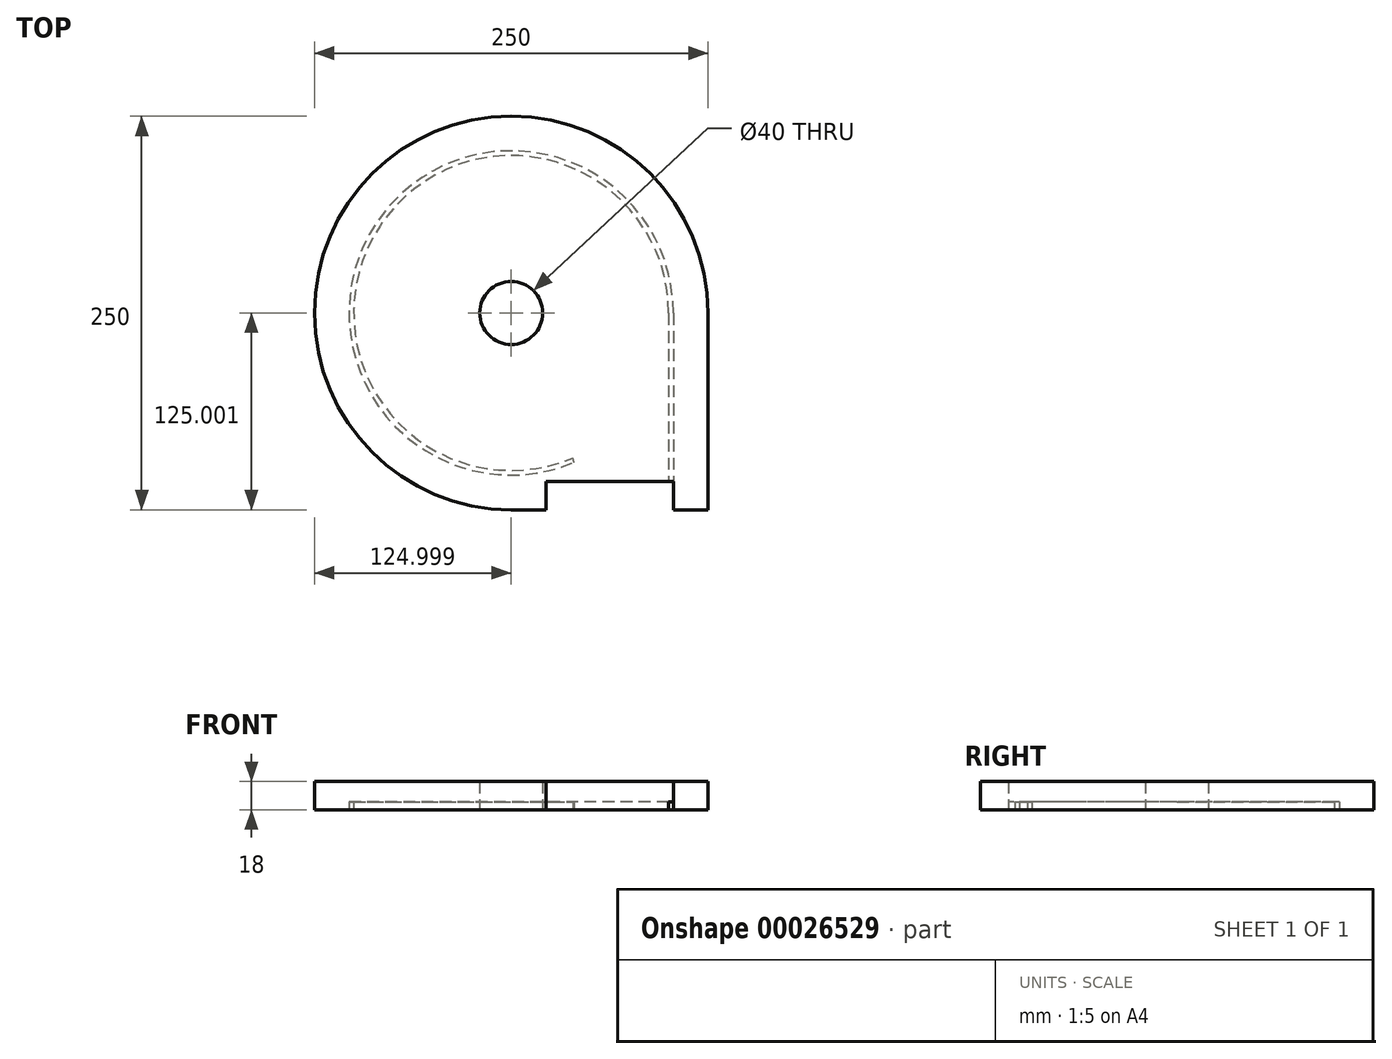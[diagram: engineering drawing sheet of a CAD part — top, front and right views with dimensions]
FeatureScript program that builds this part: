
annotation { "Feature Type Name" : "Feature", "Feature Type Description" : "" }
export const myFeature = defineFeature(function(context is Context, id is Id, definition is map)
    precondition{}
    {
        {
            var Q0;
            Q0=qCreatedBy(makeId("Top.planeOp"),FACE);
            var sketch = newSketch(context, id + "F0", { "sketchPlane" : qUnion([Q0])});
            skArc(sketch, "E0", {"start": v(5.4, 119.39) * mm, "mid": v(-133.76, 46.22) * mm, "end": v(-14.35, -56.06) * mm});
            skArc(sketch, "E1", {"start": v(60.64, 35.6) * mm, "mid": v(-122.78, 90.74) * mm, "end": v(-0.2, -56.42) * mm});
            skLineSegment(sketch, "E2", {"start": v(63.64, 35.6) * mm, "end": v(63.64, -89.4) * mm});
            skLineSegment(sketch, "E3", {"start": v(60.64, 35.6) * mm, "end": v(60.64, -71.4) * mm});
            skLineSegment(sketch, "E4", {"start": v(-17.36, -65.03) * mm, "end": v(-17.36, -89.4) * mm});
            skLineSegment(sketch, "E5", {"start": v(63.64, -71.4) * mm, "end": v(-17.36, -71.4) * mm});
            skLineSegment(sketch, "E6", {"start": v(85.64, 35.6) * mm, "end": v(85.53, -89.4) * mm});
            skLineSegment(sketch, "E7", {"start": v(-6.5, -39.68) * mm, "end": v(-6.91, -38.75) * mm});
            skLineSegment(sketch, "E8", {"start": v(8.8, 100.86) * mm, "end": v(9.4, 101.68) * mm});
            skArc(sketch, "E9", {"start": v(-6.5, 97.4) * mm, "mid": v(-108.92, 43.42) * mm, "end": v(-21.05, -31.97) * mm});
            skPoint(sketch, "E10.visualSharp", {"position": v(17.04, 112.03) * mm});
            skArc(sketch, "E10.filletArc", {"start": v(9.4, 101.68) * mm, "mid": v(11.45, 111.45) * mm, "end": v(5.4, 119.39) * mm});
            skPoint(sketch, "E11.visualSharp", {"position": v(2.2, 91.92) * mm});
            skArc(sketch, "E11.filletArc", {"start": v(-6.5, 97.4) * mm, "mid": v(1.8, 96.29) * mm, "end": v(8.8, 100.86) * mm});
            skPoint(sketch, "E12.visualSharp", {"position": v(-11.36, -28.57) * mm});
            skArc(sketch, "E12.filletArc", {"start": v(-6.91, -38.75) * mm, "mid": v(-12.72, -32.73) * mm, "end": v(-21.05, -31.97) * mm});
            skPoint(sketch, "E13.visualSharp", {"position": v(-1.36, -51.48) * mm});
            skArc(sketch, "E13.filletArc", {"start": v(-14.35, -56.06) * mm, "mid": v(-6.68, -49.66) * mm, "end": v(-6.5, -39.68) * mm});
            skLineSegment(sketch, "E14", {"start": v(0.64, -59.32) * mm, "end": v(-0.2, -56.42) * mm});
            skArc(sketch, "E15", {"start": v(85.64, 35.37) * mm, "mid": v(-127.67, 124.06) * mm, "end": v(-39.36, -89.4) * mm});
            skLineSegment(sketch, "E16", {"start": v(-39.36, -89.4) * mm, "end": v(-17.36, -89.4) * mm});
            skLineSegment(sketch, "E17", {"start": v(-17.36, -89.4) * mm, "end": v(85.53, -89.4) * mm});
            skLineSegment(sketch, "E18", {"start": v(60.64, -53.4) * mm, "end": v(12.49, -53.4) * mm});
            skArc(sketch, "E19", {"start": v(63.64, 35.6) * mm, "mid": v(-141.6, 48.02) * mm, "end": v(60.64, 10.91) * mm});
            skCircle(sketch, "E20", {"center": v(-39.36, 35.6) * mm, "radius": 20 * mm});
            skSolve(sketch);
        }
        {
            var Q0;
            {var subQ5=sQuery(id+"F0.wireOp",EDGE,"E16");Q0=makeQuery(id+"F0.imprint","IMPRINT",FACE,{"disambiguationData":[TD([[makeQuery(id+"F0.imprint","IMPRINT",EDGE,{"derivedFrom":subQ5}),1.0]])]});}
            var Q1;
            {var subQ0=sQuery(id+"F0.wireOp",EDGE,"E17");var subQ3=sQuery(id+"F0.wireOp",EDGE,"E2");var subQ4=makeQuery(id+"F0.imprint","INTERSECT",VERTEX,{"derivedFrom":[subQ3,subQ0]});Q1=makeQuery(id+"F0.imprint","IMPRINT",FACE,{"disambiguationData":[TD([[makeQuery(id+"F0.imprint","IMPRINT",EDGE,{"disambiguationData":[TD([[subQ4,1.0]])],"derivedFrom":subQ3}),-1.0]])]});}
            var Q2;
            Q2=makeQuery(id+"F0.imprint","IMPRINT",FACE,{"disambiguationData":[TD([[makeQuery(id+"F0.imprint","IMPRINT",EDGE,{"derivedFrom":sQuery(id+"F0.wireOp",EDGE,"E0")}),1.0]])]});
            var Q3;
            {var subQ3=sQuery(id+"F0.wireOp",EDGE,"E18");Q3=makeQuery(id+"F0.imprint","IMPRINT",FACE,{"disambiguationData":[TD([[makeQuery(id+"F0.imprint","IMPRINT",EDGE,{"derivedFrom":subQ3}),-1.0]])]});}
            var Q4;
            Q4=makeQuery(id+"F0.imprint","IMPRINT",FACE,{"disambiguationData":[TD([[makeQuery(id+"F0.imprint","IMPRINT",EDGE,{"derivedFrom":sQuery(id+"F0.wireOp",EDGE,"E0")}),-1.0]])]});
            var Q5;
            {var subQ6=sQuery(id+"F0.wireOp",EDGE,"E1");Q5=makeQuery(id+"F0.imprint","IMPRINT",FACE,{"disambiguationData":[TD([[makeQuery(id+"F0.imprint","IMPRINT",EDGE,{"derivedFrom":subQ6}),-1.0]])]});}
            var Q6;
            {var subQ0=sQuery(id+"F0.wireOp",EDGE,"E19");var subQ3=sQuery(id+"F0.wireOp",EDGE,"E2");var subQ4=makeQuery(id+"F0.imprint","INTERSECT",VERTEX,{"derivedFrom":[subQ3,subQ0]});Q6=makeQuery(id+"F0.imprint","IMPRINT",FACE,{"disambiguationData":[TD([[makeQuery(id+"F0.imprint","IMPRINT",EDGE,{"disambiguationData":[TD([[subQ4,-1.0]])],"derivedFrom":subQ3}),-1.0]])]});}
            var Q7;
            {var subQ1=sQuery(id+"F0.wireOp",EDGE,"E18");Q7=makeQuery(id+"F0.imprint","IMPRINT",FACE,{"disambiguationData":[TD([[makeQuery(id+"F0.imprint","IMPRINT",EDGE,{"derivedFrom":subQ1}),1.0]])]});}
            extrude(context, id + "F1", {"entities" : qUnion([Q0, Q1, Q2, Q3, Q4, Q5, Q6, Q7]), "depth" : 18 * mm});
        }
        {
            var Q0;
            {var subQ6=sQuery(id+"F0.wireOp",EDGE,"E1");Q0=makeQuery(id+"F0.imprint","IMPRINT",FACE,{"disambiguationData":[TD([[makeQuery(id+"F0.imprint","IMPRINT",EDGE,{"derivedFrom":subQ6}),-1.0]])]});}
            extrude(context, id + "F2", {"entities" : qUnion([Q0]), "operationType" : NewBodyOperationType.REMOVE, "depth" : 5 * mm});
        }
    });
